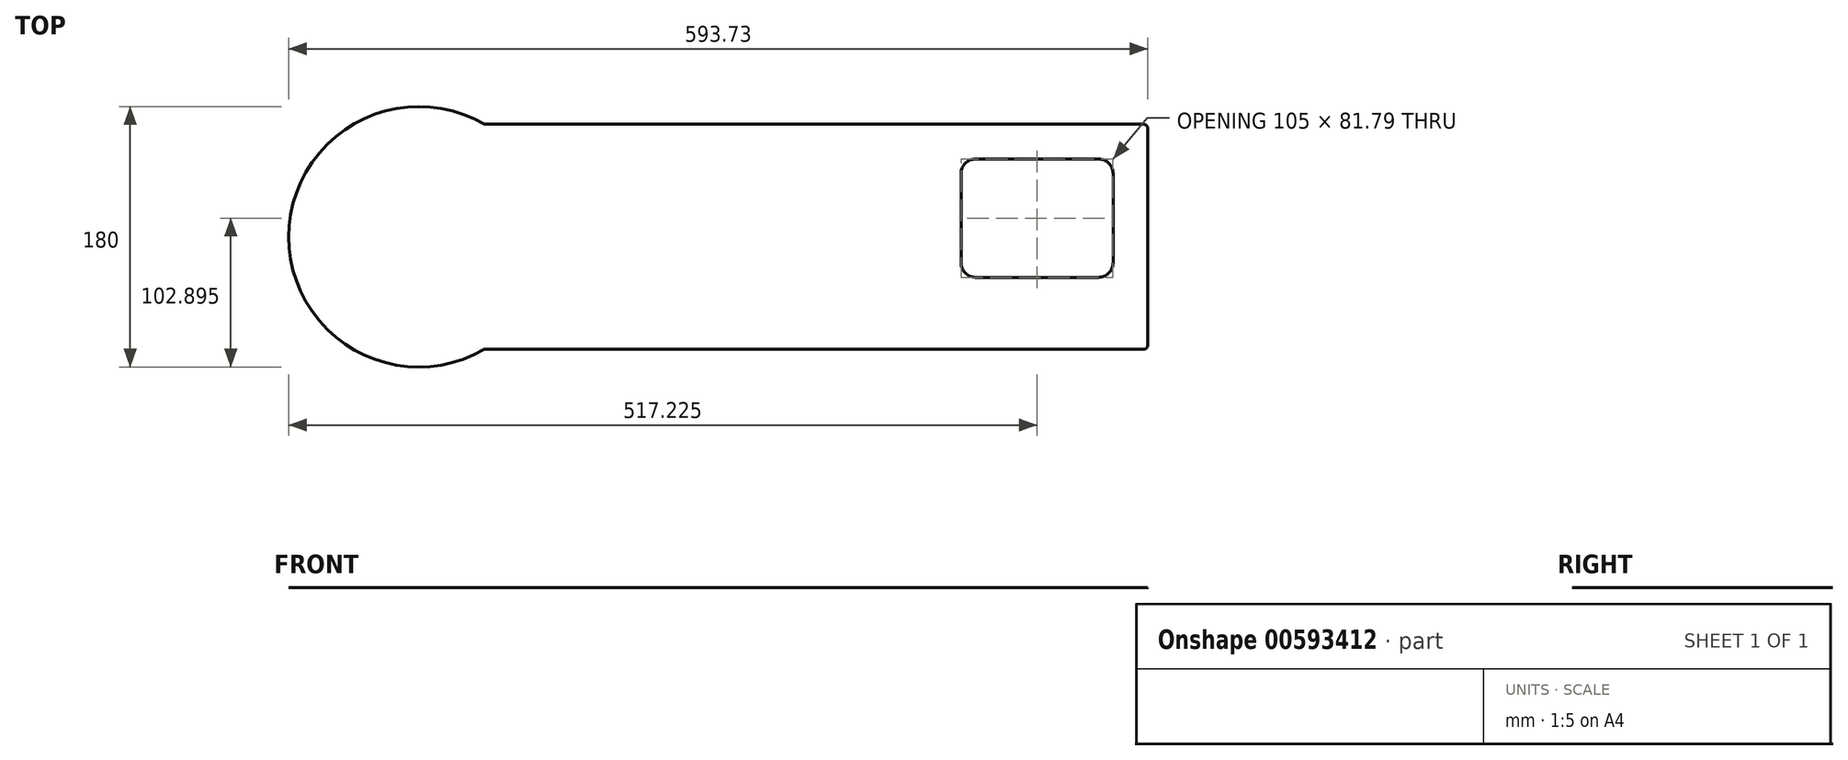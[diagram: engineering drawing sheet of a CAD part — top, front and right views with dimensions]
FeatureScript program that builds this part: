
annotation { "Feature Type Name" : "Feature", "Feature Type Description" : "" }
export const myFeature = defineFeature(function(context is Context, id is Id, definition is map)
    precondition{}
    {
        {
            var Q0;
            Q0=qCreatedBy(makeId("Top.planeOp"),FACE);
            var sketch = newSketch(context, id + "F0", { "sketchPlane" : qUnion([Q0])});
            skLineSegment(sketch, "E0.bottom", {"start": v(275.58, 77.8) * mm, "end": v(-275.59, 77.8) * mm});
            skLineSegment(sketch, "E0.top", {"start": v(275.59, -77.8) * mm, "end": v(-275.59, -77.8) * mm});
            skLineSegment(sketch, "E0.left", {"start": v(275.59, 77.8) * mm, "end": v(275.59, -77.8) * mm});
            skLineSegment(sketch, "E0.right", {"start": v(-275.59, 77.8) * mm, "end": v(-275.59, -77.8) * mm});
            skPoint(sketch, "E0.middle", {"position": v(0, 0) * mm});
            skSolve(sketch);
        }
        {
            var Q0;
            Q0 = qSketchRegion(id + "F0", true);
            extrude(context, id + "F1", {"entities" : qUnion([Q0]), "depth" : 3 / 812.8 * mm, "offsetDistance" : 25 * mm});
        }
        {
            var Q0;
            Q0=makeQuery(id+"F1.opExtrude","SWEPT_EDGE",EDGE,{"disambiguationData":[OSD([sQuery(id+"F0.wireOp",EDGE,"E0.top"),sQuery(id+"F0.wireOp",EDGE,"E0.left")])]});
            var Q1;
            Q1=makeQuery(id+"F1.opExtrude","SWEPT_EDGE",EDGE,{"disambiguationData":[OSD([sQuery(id+"F0.wireOp",EDGE,"E0.top"),sQuery(id+"F0.wireOp",EDGE,"E0.right")])]});
            var Q2;
            Q2=makeQuery(id+"F1.opExtrude","SWEPT_EDGE",EDGE,{"disambiguationData":[OSD([sQuery(id+"F0.wireOp",EDGE,"E0.bottom"),sQuery(id+"F0.wireOp",EDGE,"E0.right")])]});
            var Q3;
            Q3=makeQuery(id+"F1.opExtrude","SWEPT_EDGE",EDGE,{"disambiguationData":[OSD([sQuery(id+"F0.wireOp",EDGE,"E0.bottom"),sQuery(id+"F0.wireOp",EDGE,"E0.left")])]});
            fillet(context, id + "F2", {"entities" : qUnion([Q0, Q1, Q2, Q3]), "radius" : 3 * mm, "tangentPropagation" : true, "allowEdgeOverflow" : false});
        }
        {
            var Q0;
            Q0=makeQuery(id+"F1.opExtrude","CAP_FACE",FACE,{"disambiguationData":[OSD([sQuery(id+"F0.wireOp",EDGE,"E0.bottom"),sQuery(id+"F0.wireOp",EDGE,"E0.top"),sQuery(id+"F0.wireOp",EDGE,"E0.left"),sQuery(id+"F0.wireOp",EDGE,"E0.right")])],"isStart":false});
            var sketch = newSketch(context, id + "F3", { "sketchPlane" : qUnion([Q0])});
            skLineSegment(sketch, "E1.bottom", {"start": v(251.59, 53.8) * mm, "end": v(146.59, 53.8) * mm});
            skLineSegment(sketch, "E1.top", {"start": v(251.59, -28) * mm, "end": v(146.59, -28) * mm});
            skLineSegment(sketch, "E1.left", {"start": v(251.59, 53.8) * mm, "end": v(251.59, -28) * mm});
            skLineSegment(sketch, "E1.right", {"start": v(146.59, 53.8) * mm, "end": v(146.59, -28) * mm});
            skPoint(sketch, "E1.middle", {"position": v(199.09, 12.9) * mm});
            skSolve(sketch);
        }
        {
            var Q0;
            Q0 = qSketchRegion(id + "F3", true);
            extrude(context, id + "F4", {"entities" : qUnion([Q0]), "operationType" : NewBodyOperationType.REMOVE, "oppositeDirection" : true, "depth" : 25 * mm, "offsetDistance" : 25 * mm});
        }
        {
            var Q0;
            Q0=makeQuery(id+"F4.boolean.opBoolean","COPY",EDGE,{"derivedFrom":makeQuery(id+"F4.opExtrude","SWEPT_EDGE",EDGE,{"disambiguationData":[OSD([sQuery(id+"F3.wireOp",EDGE,"E1.bottom"),sQuery(id+"F3.wireOp",EDGE,"E1.right")])]})});
            var Q1;
            Q1=makeQuery(id+"F4.boolean.opBoolean","COPY",EDGE,{"derivedFrom":makeQuery(id+"F4.opExtrude","SWEPT_EDGE",EDGE,{"disambiguationData":[OSD([sQuery(id+"F3.wireOp",EDGE,"E1.top"),sQuery(id+"F3.wireOp",EDGE,"E1.right")])]})});
            var Q2;
            Q2=makeQuery(id+"F4.boolean.opBoolean","COPY",EDGE,{"derivedFrom":makeQuery(id+"F4.opExtrude","SWEPT_EDGE",EDGE,{"disambiguationData":[OSD([sQuery(id+"F3.wireOp",EDGE,"E1.bottom"),sQuery(id+"F3.wireOp",EDGE,"E1.left")])]})});
            var Q3;
            Q3=makeQuery(id+"F4.boolean.opBoolean","COPY",EDGE,{"derivedFrom":makeQuery(id+"F4.opExtrude","SWEPT_EDGE",EDGE,{"disambiguationData":[OSD([sQuery(id+"F3.wireOp",EDGE,"E1.top"),sQuery(id+"F3.wireOp",EDGE,"E1.left")])]})});
            fillet(context, id + "F5", {"entities" : qUnion([Q0, Q1, Q2, Q3]), "radius" : 10 * mm, "tangentPropagation" : true, "allowEdgeOverflow" : false});
        }
        {
            var Q0;
            Q0=makeQuery(id+"F1.opExtrude","CAP_FACE",FACE,{"disambiguationData":[OSD([sQuery(id+"F0.wireOp",EDGE,"E0.bottom"),sQuery(id+"F0.wireOp",EDGE,"E0.top"),sQuery(id+"F0.wireOp",EDGE,"E0.left"),sQuery(id+"F0.wireOp",EDGE,"E0.right")])],"isStart":false});
            var sketch = newSketch(context, id + "F6", { "sketchPlane" : qUnion([Q0])});
            skCircle(sketch, "E2", {"center": v(-228.14, 0) * mm, "radius": 90 * mm});
            skSolve(sketch);
        }
        {
            var Q0;
            Q0 = qSketchRegion(id + "F6", true);
            var Q1;
            Q1=makeQuery(id+"F1.opExtrude","CAP_FACE",FACE,{"disambiguationData":[OSD([sQuery(id+"F0.wireOp",EDGE,"E0.bottom"),sQuery(id+"F0.wireOp",EDGE,"E0.top"),sQuery(id+"F0.wireOp",EDGE,"E0.left"),sQuery(id+"F0.wireOp",EDGE,"E0.right")])],"isStart":true});
            extrude(context, id + "F7", {"entities" : qUnion([Q0]), "operationType" : NewBodyOperationType.ADD, "endBound" : BoundingType.UP_TO_SURFACE, "oppositeDirection" : true, "depth" : 25 * mm, "endBoundEntityFace" : qUnion([Q1]), "offsetDistance" : 25 * mm});
        }
    });
